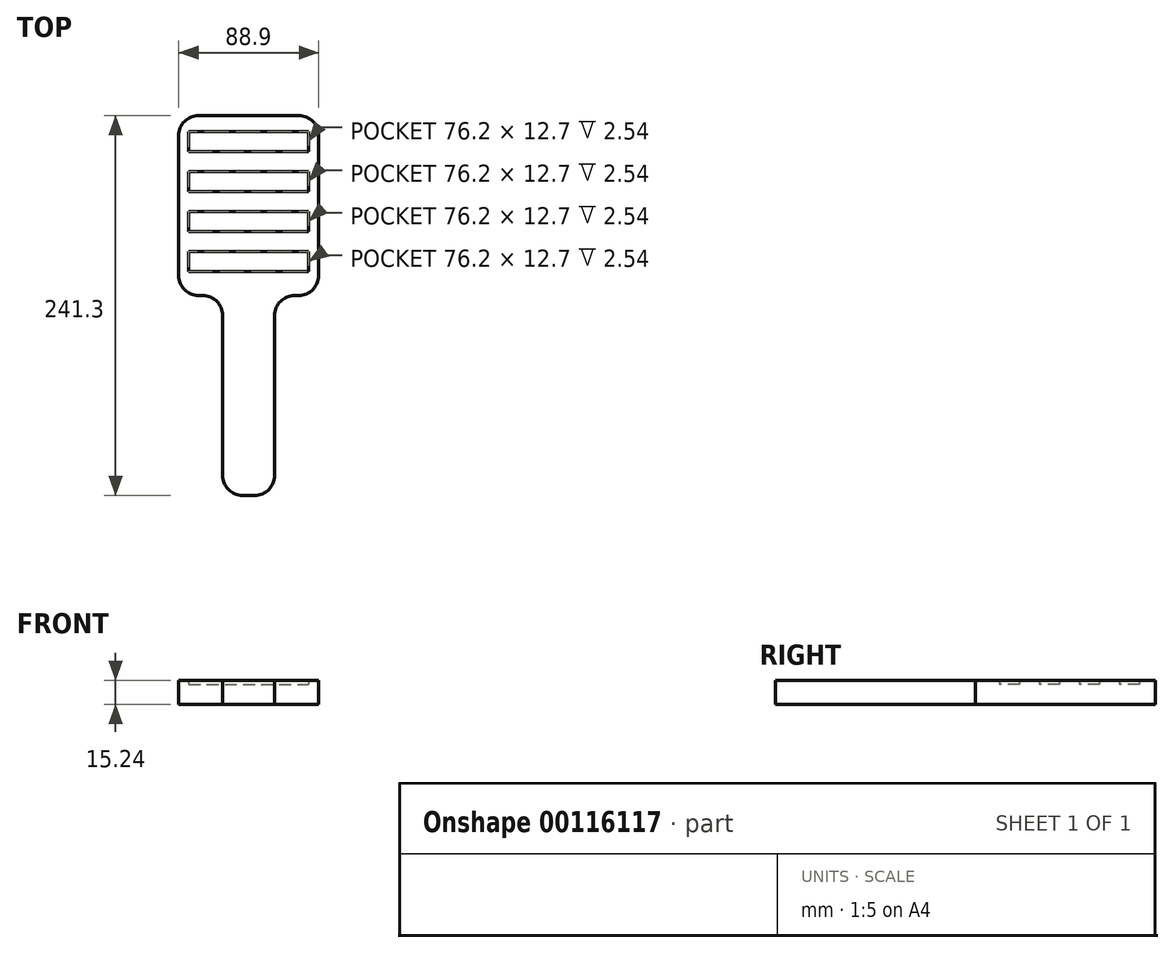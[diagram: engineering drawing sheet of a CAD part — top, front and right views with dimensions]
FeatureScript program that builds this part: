
annotation { "Feature Type Name" : "Feature", "Feature Type Description" : "" }
export const myFeature = defineFeature(function(context is Context, id is Id, definition is map)
    precondition{}
    {
        {
            var Q0;
            Q0=qCreatedBy(makeId("Top.planeOp"),FACE);
            var sketch = newSketch(context, id + "F0", { "sketchPlane" : qUnion([Q0])});
            skLineSegment(sketch, "E0.bottom", {"start": v(31.75, 57.15) * mm, "end": v(-31.75, 57.15) * mm});
            skPoint(sketch, "E0.middle", {"position": v(0, 0) * mm});
            skLineSegment(sketch, "E1.top", {"start": v(-3.81, -184.15) * mm, "end": v(3.81, -184.15) * mm});
            skLineSegment(sketch, "E1.right", {"start": v(16.51, -85.1) * mm, "end": v(16.5, -171.45) * mm});
            skPoint(sketch, "E2", {"position": v(0, -184.15) * mm});
            skPoint(sketch, "E3", {"position": v(-16.5, -85.1) * mm});
            skPoint(sketch, "E4.MirrorP", {"position": v(16.5, -85.1) * mm});
            skPoint(sketch, "E5", {"position": v(-30.87, -61.8) * mm});
            skPoint(sketch, "E6.MirrorP", {"position": v(30.87, -61.8) * mm});
            skPoint(sketch, "E7", {"position": v(-44.45, -50.04) * mm});
            skPoint(sketch, "E8.orphan", {"position": v(-44.45, -57.15) * mm});
            skPoint(sketch, "E9.orphan", {"position": v(44.45, -57.15) * mm});
            skPoint(sketch, "E10.visualSharp", {"position": v(-44.45, 57.15) * mm});
            skArc(sketch, "E10.filletArc", {"start": v(-31.75, 57.15) * mm, "mid": v(-40.73, 53.43) * mm, "end": v(-44.45, 44.45) * mm});
            skPoint(sketch, "E11.visualSharp", {"position": v(44.45, 57.15) * mm});
            skArc(sketch, "E11.filletArc", {"start": v(44.45, 44.45) * mm, "mid": v(40.73, 53.43) * mm, "end": v(31.75, 57.15) * mm});
            skPoint(sketch, "E12.visualSharp", {"position": v(-16.51, -184.15) * mm});
            skArc(sketch, "E12.filletArc", {"start": v(-16.51, -171.45) * mm, "mid": v(-12.8, -180.43) * mm, "end": v(-3.81, -184.15) * mm});
            skPoint(sketch, "E13.visualSharp", {"position": v(16.51, -184.15) * mm});
            skArc(sketch, "E13.filletArc", {"start": v(3.81, -184.15) * mm, "mid": v(12.8, -180.43) * mm, "end": v(16.51, -171.45) * mm});
            skPoint(sketch, "E1.bottom.start.orphan", {"position": v(-16.5, -57.15) * mm});
            skLineSegment(sketch, "E14", {"start": v(16.51, -85.1) * mm, "end": v(16.51, -72.4) * mm});
            skPoint(sketch, "E0.left.start.orphan", {"position": v(44.45, -50.04) * mm});
            skLineSegment(sketch, "E15", {"start": v(44.45, 44.45) * mm, "end": v(44.45, -44.45) * mm});
            skLineSegment(sketch, "E16", {"start": v(-44.45, 44.45) * mm, "end": v(-44.45, -44.45) * mm});
            skLineSegment(sketch, "E17", {"start": v(-31.75, -57.15) * mm, "end": v(-29.2, -57.15) * mm});
            skLineSegment(sketch, "E18", {"start": v(-16.5, -69.85) * mm, "end": v(-16.51, -171.45) * mm});
            skArc(sketch, "E19.filletArc", {"start": v(-16.5, -69.85) * mm, "mid": v(-20.23, -60.87) * mm, "end": v(-29.2, -57.15) * mm});
            skArc(sketch, "E20.filletArc", {"start": v(-44.45, -44.45) * mm, "mid": v(-40.73, -53.43) * mm, "end": v(-31.75, -57.15) * mm});
            skArc(sketch, "E21.MirrorCS", {"start": v(44.45, -44.45) * mm, "mid": v(40.73, -53.43) * mm, "end": v(31.75, -57.15) * mm});
            skArc(sketch, "E22.MirrorCS", {"start": v(16.5, -69.85) * mm, "mid": v(20.23, -60.87) * mm, "end": v(29.2, -57.15) * mm});
            skLineSegment(sketch, "E23", {"start": v(29.2, -57.15) * mm, "end": v(31.75, -57.15) * mm});
            skLineSegment(sketch, "E24", {"start": v(16.5, -69.85) * mm, "end": v(16.51, -72.4) * mm});
            skLineSegment(sketch, "E25.bottom", {"start": v(-38.1, 46.99) * mm, "end": v(38.1, 46.99) * mm});
            skLineSegment(sketch, "E25.top", {"start": v(-38.1, 34.29) * mm, "end": v(38.1, 34.29) * mm});
            skLineSegment(sketch, "E25.left", {"start": v(-38.1, 47) * mm, "end": v(-38.1, 34.3) * mm});
            skLineSegment(sketch, "E25.right", {"start": v(38.1, 47) * mm, "end": v(38.1, 34.3) * mm});
            skLineSegment(sketch, "E26.1.0.4", {"start": v(-38.1, 21.59) * mm, "end": v(38.1, 21.59) * mm});
            skLineSegment(sketch, "E26.1.0.5", {"start": v(-38.1, 21.59) * mm, "end": v(-38.1, 8.89) * mm});
            skLineSegment(sketch, "E26.1.0.6", {"start": v(-38.1, 8.89) * mm, "end": v(38.1, 8.89) * mm});
            skLineSegment(sketch, "E26.1.0.7", {"start": v(38.1, 21.59) * mm, "end": v(38.1, 8.89) * mm});
            skLineSegment(sketch, "E26.2.0.4", {"start": v(-38.1, -3.81) * mm, "end": v(38.1, -3.81) * mm});
            skLineSegment(sketch, "E26.2.0.5", {"start": v(-38.1, -3.81) * mm, "end": v(-38.1, -16.51) * mm});
            skLineSegment(sketch, "E26.2.0.6", {"start": v(-38.1, -16.51) * mm, "end": v(38.1, -16.51) * mm});
            skLineSegment(sketch, "E26.2.0.7", {"start": v(38.1, -3.81) * mm, "end": v(38.1, -16.51) * mm});
            skLineSegment(sketch, "E26.3.0.4", {"start": v(-38.1, -29.21) * mm, "end": v(38.1, -29.21) * mm});
            skLineSegment(sketch, "E26.3.0.5", {"start": v(-38.1, -29.21) * mm, "end": v(-38.1, -41.91) * mm});
            skLineSegment(sketch, "E26.3.0.6", {"start": v(-38.1, -41.91) * mm, "end": v(38.1, -41.91) * mm});
            skLineSegment(sketch, "E26.3.0.7", {"start": v(38.1, -29.21) * mm, "end": v(38.1, -41.91) * mm});
            skSolve(sketch);
        }
        {
            var Q0;
            Q0=qCreatedBy(makeId("Top.planeOp"),FACE);
            var sketch = newSketch(context, id + "F1", { "sketchPlane" : qUnion([Q0])});
            skLineSegment(sketch, "E27.bottom", {"start": v(-38.1, 44.45) * mm, "end": v(38.1, 44.45) * mm});
            skLineSegment(sketch, "E27.top", {"start": v(-38.1, 31.75) * mm, "end": v(38.1, 31.75) * mm});
            skLineSegment(sketch, "E27.left", {"start": v(-38.1, 44.45) * mm, "end": v(-38.1, 31.75) * mm});
            skLineSegment(sketch, "E27.right", {"start": v(38.1, 44.45) * mm, "end": v(38.1, 31.75) * mm});
            skLineSegment(sketch, "E28.1.0.4", {"start": v(-38.1, 19.05) * mm, "end": v(38.1, 19.05) * mm});
            skLineSegment(sketch, "E28.1.0.5", {"start": v(-38.1, 19.05) * mm, "end": v(-38.1, 6.35) * mm});
            skLineSegment(sketch, "E28.1.0.6", {"start": v(-38.1, 6.35) * mm, "end": v(38.1, 6.35) * mm});
            skLineSegment(sketch, "E28.1.0.7", {"start": v(38.1, 19.05) * mm, "end": v(38.1, 6.35) * mm});
            skLineSegment(sketch, "E28.2.0.4", {"start": v(-38.1, -6.35) * mm, "end": v(38.1, -6.35) * mm});
            skLineSegment(sketch, "E28.2.0.5", {"start": v(-38.1, -6.35) * mm, "end": v(-38.1, -19.05) * mm});
            skLineSegment(sketch, "E28.2.0.6", {"start": v(-38.1, -19.05) * mm, "end": v(38.1, -19.05) * mm});
            skLineSegment(sketch, "E28.2.0.7", {"start": v(38.1, -6.35) * mm, "end": v(38.1, -19.05) * mm});
            skLineSegment(sketch, "E28.3.0.4", {"start": v(-38.1, -31.75) * mm, "end": v(38.1, -31.75) * mm});
            skLineSegment(sketch, "E28.3.0.5", {"start": v(-38.1, -31.75) * mm, "end": v(-38.1, -44.45) * mm});
            skLineSegment(sketch, "E28.3.0.6", {"start": v(-38.1, -44.45) * mm, "end": v(38.1, -44.45) * mm});
            skLineSegment(sketch, "E28.3.0.7", {"start": v(38.1, -31.75) * mm, "end": v(38.1, -44.45) * mm});
            skSolve(sketch);
        }
        {
            var Q0;
            Q0=makeQuery(id+"F0.imprint","IMPRINT",FACE,{"disambiguationData":[TD([[makeQuery(id+"F0.imprint","IMPRINT",EDGE,{"derivedFrom":sQuery(id+"F0.wireOp",EDGE,"E0.bottom")}),1.0]])]});
            extrude(context, id + "F2", {"entities" : qUnion([Q0]), "depth" : 15.24 * mm});
        }
        {
            var Q0;
            Q0=makeQuery(id+"F0.imprint","IMPRINT",FACE,{"disambiguationData":[TD([[makeQuery(id+"F0.imprint","IMPRINT",EDGE,{"derivedFrom":sQuery(id+"F0.wireOp",EDGE,"E25.bottom")}),-1.0]])]});
            var Q1;
            Q1=makeQuery(id+"F0.imprint","IMPRINT",FACE,{"disambiguationData":[TD([[makeQuery(id+"F0.imprint","IMPRINT",EDGE,{"derivedFrom":sQuery(id+"F0.wireOp",EDGE,"E26.1.0.4")}),-1.0]])]});
            var Q2;
            Q2=makeQuery(id+"F0.imprint","IMPRINT",FACE,{"disambiguationData":[TD([[makeQuery(id+"F0.imprint","IMPRINT",EDGE,{"derivedFrom":sQuery(id+"F0.wireOp",EDGE,"E26.2.0.4")}),-1.0]])]});
            var Q3;
            Q3=makeQuery(id+"F0.imprint","IMPRINT",FACE,{"disambiguationData":[TD([[makeQuery(id+"F0.imprint","IMPRINT",EDGE,{"derivedFrom":sQuery(id+"F0.wireOp",EDGE,"E26.3.0.4")}),-1.0]])]});
            extrude(context, id + "F3", {"entities" : qUnion([Q0, Q1, Q2, Q3]), "operationType" : NewBodyOperationType.ADD, "depth" : 12.7 * mm});
        }
    });
